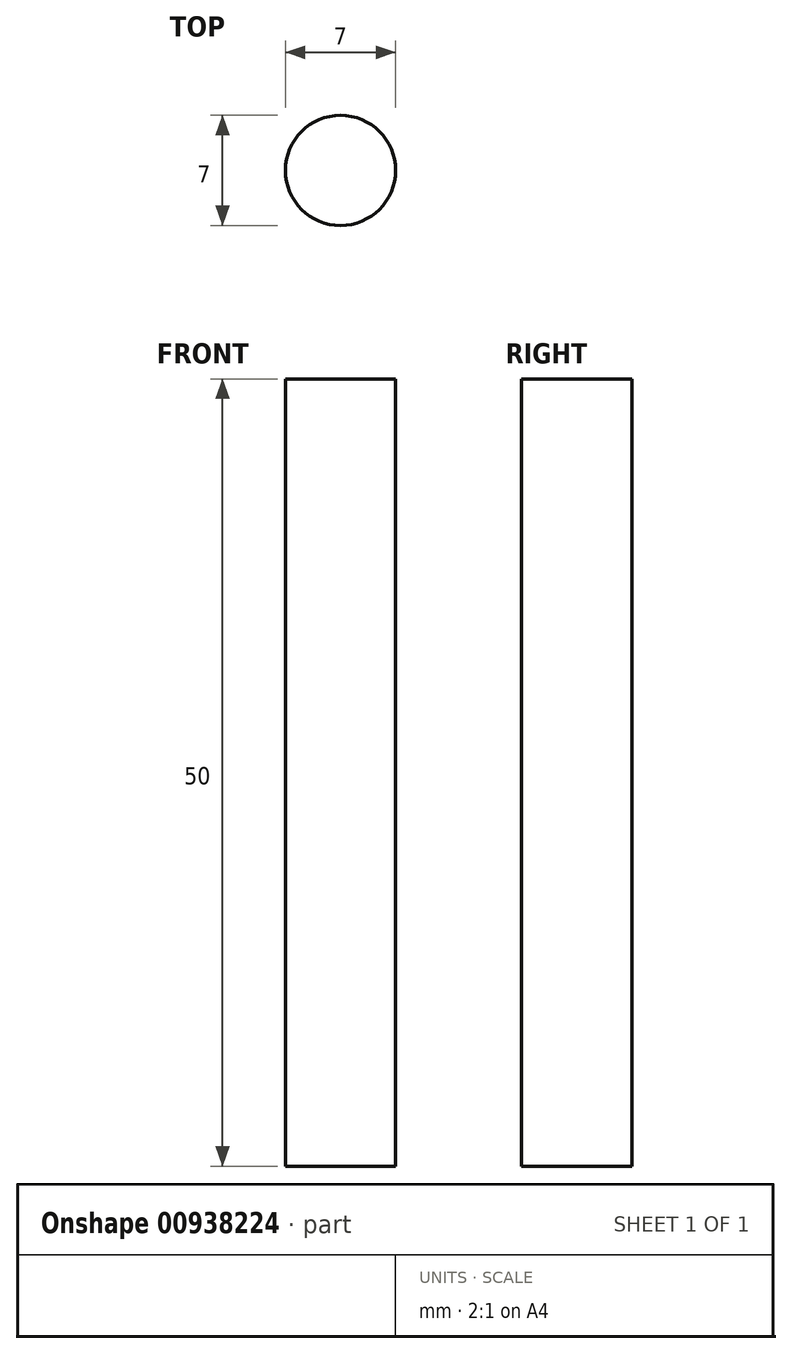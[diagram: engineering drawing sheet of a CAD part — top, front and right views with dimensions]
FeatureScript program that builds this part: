
annotation { "Feature Type Name" : "Feature", "Feature Type Description" : "" }
export const myFeature = defineFeature(function(context is Context, id is Id, definition is map)
    precondition{}
    {
        {
            var Q0;
            Q0=qCreatedBy(makeId("Top.planeOp"),FACE);
            var sketch = newSketch(context, id + "F0", { "sketchPlane" : qUnion([Q0])});
            skCircle(sketch, "E0", {"center": v(0, 0) * mm, "radius": 3.5 * mm});
            skSolve(sketch);
        }
        {
            var Q0;
            Q0=makeQuery(id+"F0.imprint","IMPRINT",FACE,{"disambiguationData":[TD([[makeQuery(id+"F0.imprint","IMPRINT",EDGE,{"derivedFrom":sQuery(id+"F0.wireOp",EDGE,"E0")}),1.0]])]});
            extrude(context, id + "F1", {"entities" : qUnion([Q0]), "depth" : 50 * mm, "offsetDistance" : 25 * mm});
        }
    });
